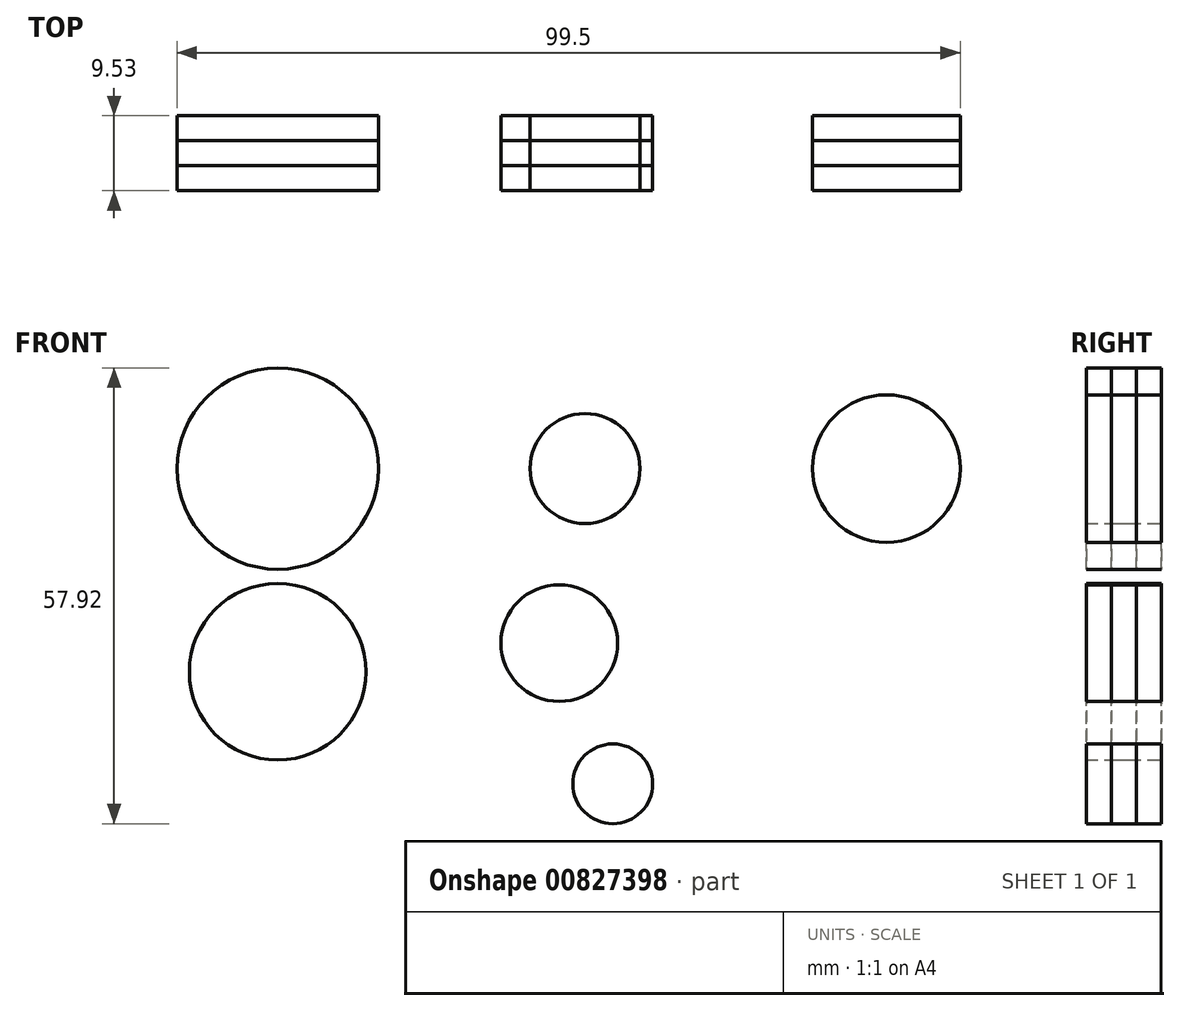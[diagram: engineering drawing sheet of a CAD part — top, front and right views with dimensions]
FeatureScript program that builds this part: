
annotation { "Feature Type Name" : "Feature", "Feature Type Description" : "" }
export const myFeature = defineFeature(function(context is Context, id is Id, definition is map)
    precondition{}
    {
        {
            var Q0;
            Q0=qCreatedBy(makeId("Front.planeOp"),FACE);
            var sketch = newSketch(context, id + "F0", { "sketchPlane" : qUnion([Q0])});
            skCircle(sketch, "E0", {"center": v(-57.3, 53.03) * mm, "radius": 12.8 * mm});
            skCircle(sketch, "E1", {"center": v(-21.54, 30.86) * mm, "radius": 7.4 * mm});
            skCircle(sketch, "E2", {"center": v(-18.26, 53.03) * mm, "radius": 6.99 * mm});
            skCircle(sketch, "E3", {"center": v(20.03, 53.03) * mm, "radius": 9.37 * mm});
            skCircle(sketch, "E4", {"center": v(-57.3, 27.2) * mm, "radius": 11.21 * mm});
            skCircle(sketch, "E5", {"center": v(-14.74, 12.97) * mm, "radius": 5.07 * mm});
            skSolve(sketch);
        }
        {
            var Q0;
            Q0=makeQuery(id+"F0.imprint","IMPRINT",FACE,{"disambiguationData":[TD([[makeQuery(id+"F0.imprint","IMPRINT",EDGE,{"derivedFrom":sQuery(id+"F0.wireOp",EDGE,"E0")}),1.0]])]});
            var Q1;
            Q1=makeQuery(id+"F0.imprint","IMPRINT",FACE,{"disambiguationData":[TD([[makeQuery(id+"F0.imprint","IMPRINT",EDGE,{"derivedFrom":sQuery(id+"F0.wireOp",EDGE,"E2")}),1.0]])]});
            var Q2;
            Q2=makeQuery(id+"F0.imprint","IMPRINT",FACE,{"disambiguationData":[TD([[makeQuery(id+"F0.imprint","IMPRINT",EDGE,{"derivedFrom":sQuery(id+"F0.wireOp",EDGE,"E1")}),1.0]])]});
            var Q3;
            Q3=makeQuery(id+"F0.imprint","IMPRINT",FACE,{"disambiguationData":[TD([[makeQuery(id+"F0.imprint","IMPRINT",EDGE,{"derivedFrom":sQuery(id+"F0.wireOp",EDGE,"E3")}),1.0]])]});
            extrude(context, id + "F1", {"entities" : qUnion([Q0, Q1, Q2, Q3]), "endBound" : BoundingType.SYMMETRIC, "depth" : 6.35 * mm, "offsetDistance" : 25.4 * mm});
        }
        {
            var Q0;
            Q0 = qSketchRegion(id + "F0", true);
            extrude(context, id + "F2", {"entities" : qUnion([Q0]), "endBound" : BoundingType.SYMMETRIC, "depth" : 6.35 * mm, "offsetDistance" : 25.4 * mm});
        }
        {
            var Q0;
            Q0 = qSketchRegion(id + "F0", true);
            extrude(context, id + "F3", {"entities" : qUnion([Q0]), "depth" : 6.35 * mm, "offsetDistance" : 25.4 * mm});
        }
    });
